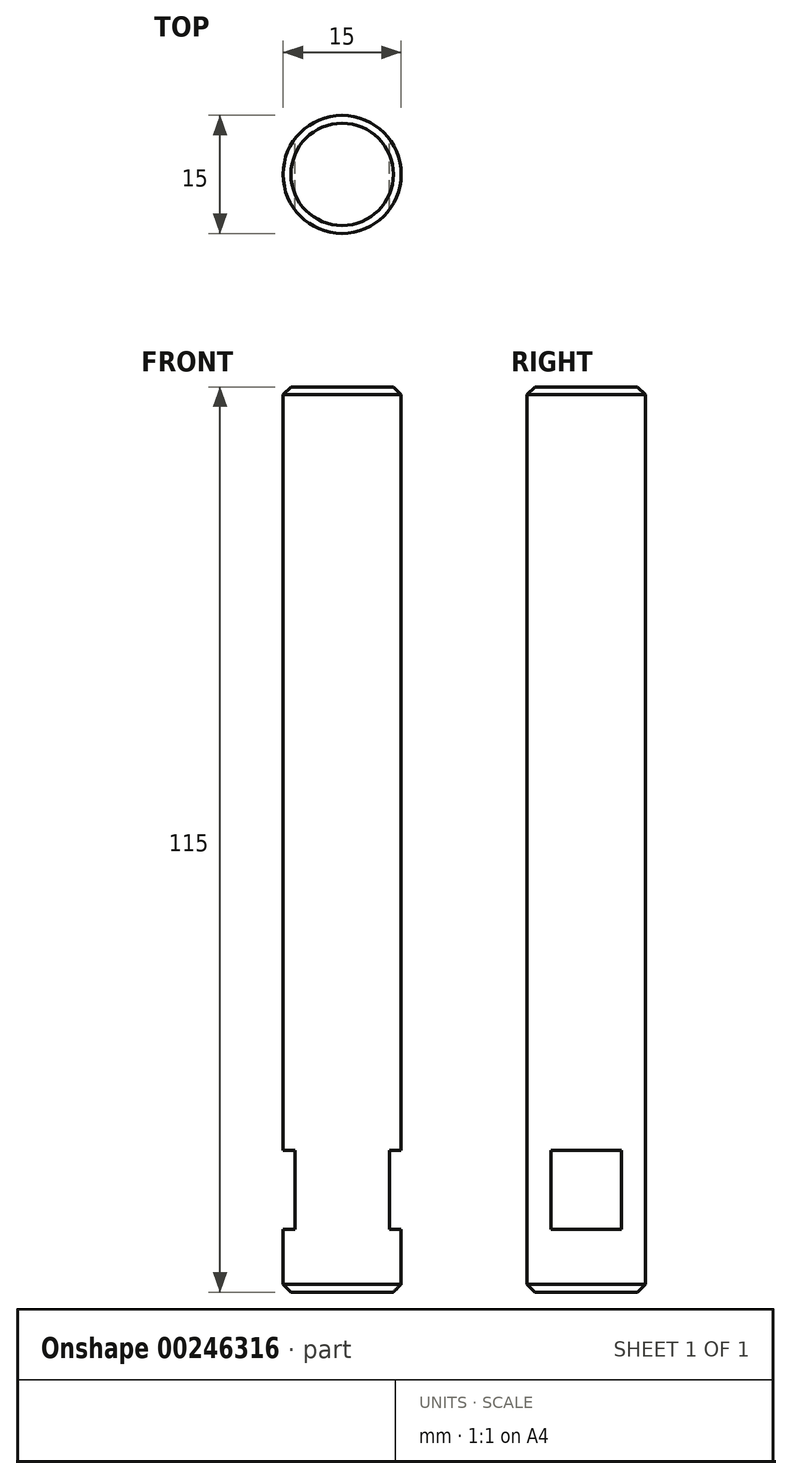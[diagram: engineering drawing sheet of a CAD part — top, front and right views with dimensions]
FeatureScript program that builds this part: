
annotation { "Feature Type Name" : "Feature", "Feature Type Description" : "" }
export const myFeature = defineFeature(function(context is Context, id is Id, definition is map)
    precondition{}
    {
        {
            var Q0;
            Q0=qCreatedBy(makeId("Top.planeOp"),FACE);
            var sketch = newSketch(context, id + "F0", { "sketchPlane" : qUnion([Q0])});
            skPoint(sketch, "E0", {"position": v(0, 0) * mm});
            skCircle(sketch, "E1", {"center": v(0, 0) * mm, "radius": 7.5 * mm});
            skSolve(sketch);
        }
        {
            var Q0;
            Q0=makeQuery(id+"F0.imprint","IMPRINT",FACE,{"disambiguationData":[TD([[makeQuery(id+"F0.imprint","IMPRINT",EDGE,{"derivedFrom":sQuery(id+"F0.wireOp",EDGE,"E1")}),1.0]])]});
            extrude(context, id + "F1", {"entities" : qUnion([Q0]), "depth" : 115 * mm});
        }
        {
            var Q0;
            Q0=makeQuery(id+"F1.opExtrude","CAP_EDGE",EDGE,{"disambiguationData":[OSD([sQuery(id+"F0.wireOp",EDGE,"E1")])],"isStart":false});
            var Q1;
            Q1=makeQuery(id+"F1.opExtrude","CAP_EDGE",EDGE,{"disambiguationData":[OSD([sQuery(id+"F0.wireOp",EDGE,"E1")])],"isStart":true});
            chamfer(context, id + "F2", {"entities" : qUnion([Q0, Q1]), "chamferType" : ChamferType.OFFSET_ANGLE, "width" : 1 * mm, "oppositeDirection" : false, "angle" : 45 * degree, "tangentPropagation" : true});
        }
        {
            var Q0;
            Q0=qCreatedBy(makeId("Front.planeOp"),FACE);
            var sketch = newSketch(context, id + "F3", { "sketchPlane" : qUnion([Q0])});
            skLineSegment(sketch, "E2", {"start": v(0, 127.76) * mm, "end": v(0, -24.56) * mm, "construction": true});
            skLineSegment(sketch, "E3", {"start": v(7.5, 114) * mm, "end": v(7.5, 0) * mm});
            skLineSegment(sketch, "E4", {"start": v(-7.5, 0) * mm, "end": v(-7.5, 114) * mm});
            skLineSegment(sketch, "E5", {"start": v(7.5, 18) * mm, "end": v(6, 18) * mm});
            skLineSegment(sketch, "E6", {"start": v(6, 18) * mm, "end": v(6, 8) * mm});
            skLineSegment(sketch, "E7", {"start": v(6, 8) * mm, "end": v(7.5, 8) * mm});
            skLineSegment(sketch, "E8", {"start": v(-7.5, 18) * mm, "end": v(-6, 18) * mm});
            skLineSegment(sketch, "E9", {"start": v(-6, 18) * mm, "end": v(-6, 8) * mm});
            skLineSegment(sketch, "E10", {"start": v(-6, 8) * mm, "end": v(-7.5, 8) * mm});
            skSolve(sketch);
        }
        {
            var Q0;
            Q0 = qSketchRegion(id + "F3", true);
            extrude(context, id + "F4", {"entities" : qUnion([Q0]), "operationType" : NewBodyOperationType.REMOVE, "endBound" : BoundingType.THROUGH_ALL, "depth" : 100 * mm, "hasSecondDirection" : true, "secondDirectionBound" : SecondDirectionBoundingType.THROUGH_ALL, "secondDirectionOppositeDirection" : true, "secondDirectionDepth" : 25 * mm});
        }
    });
